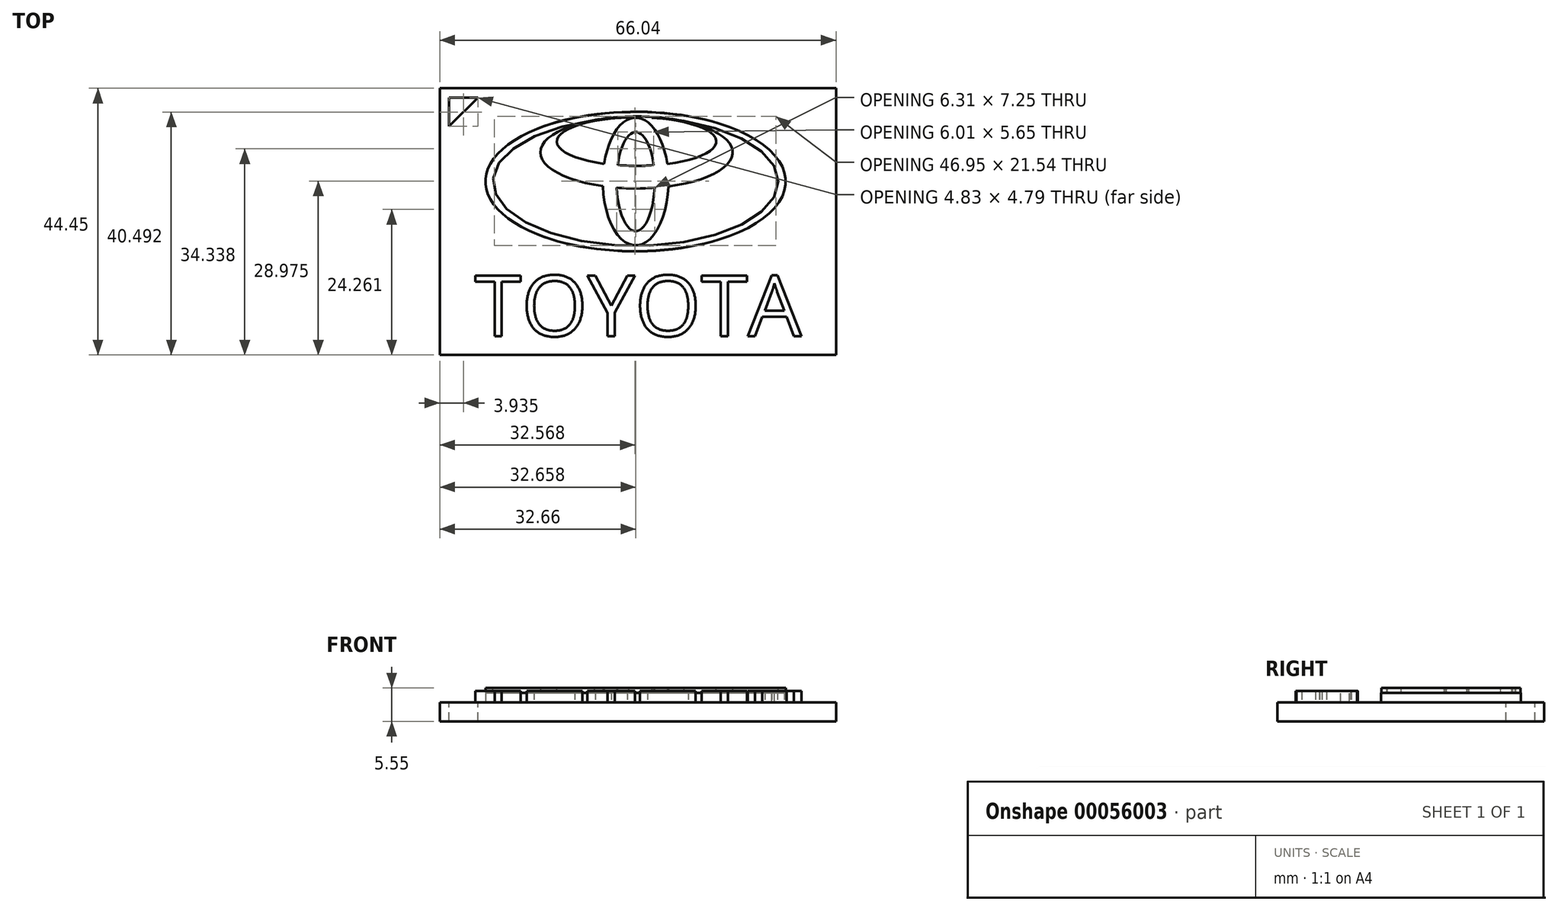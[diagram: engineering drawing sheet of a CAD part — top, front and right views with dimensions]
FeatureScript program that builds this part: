
annotation { "Feature Type Name" : "Feature", "Feature Type Description" : "" }
export const myFeature = defineFeature(function(context is Context, id is Id, definition is map)
    precondition{}
    {
        {
            var Q0;
            Q0=qCreatedBy(makeId("Top.planeOp"),FACE);
            var sketch = newSketch(context, id + "F0", { "sketchPlane" : qUnion([Q0])});
            skLineSegment(sketch, "E0.bottom", {"start": v(-29.53, -28.9) * mm, "end": v(36.5, -28.9) * mm});
            skLineSegment(sketch, "E0.top", {"start": v(-29.53, 15.55) * mm, "end": v(36.5, 15.55) * mm});
            skLineSegment(sketch, "E0.left", {"start": v(-29.53, -28.9) * mm, "end": v(-29.53, 15.55) * mm});
            skLineSegment(sketch, "E0.right", {"start": v(36.5, -28.9) * mm, "end": v(36.5, 15.55) * mm});
            skLineSegment(sketch, "E1", {"start": v(-28, 13.99) * mm, "end": v(-28, 9.2) * mm});
            skLineSegment(sketch, "E2", {"start": v(-28, 9.2) * mm, "end": v(-23.18, 13.99) * mm});
            skLineSegment(sketch, "E3", {"start": v(-23.18, 13.99) * mm, "end": v(-28, 13.99) * mm});
            skEllipse(sketch, "E4", {"center": v(3.1, 0) * mm, "majorRadius": 25.02 * mm, "minorRadius": 11.63 * mm, "majorAxis": v(-1, 0)});
            skText(sketch, "E5", { "text": "TOYOTA", "fontName": "OpenSans-Regular.ttf"});
            skPoint(sketch, "E6", {"position": v(-21.91, 0) * mm});
            skPoint(sketch, "E7", {"position": v(28.13, 0) * mm});
            const initialGuessF0  = {"E5": [-0.0237, -0.02576, 1, 0, 0.01016]};
            skSetInitialGuess(sketch, initialGuessF0);
            skSolve(sketch);
        }
        {
            var Q0;
            Q0=makeQuery(id+"F0.imprint","IMPRINT",FACE,{"disambiguationData":[TD([[makeQuery(id+"F0.imprint","IMPRINT",EDGE,{"derivedFrom":sQuery(id+"F0.wireOp",EDGE,"E0.bottom")}),1.0]])]});
            var Q1;
            Q1=makeQuery(id+"F0.imprint","IMPRINT",FACE,{"disambiguationData":[TD([[makeQuery(id+"F0.imprint","IMPRINT",EDGE,{"derivedFrom":sQuery(id+"F0.wireOp",EDGE,"E4")}),1.0]])]});
            var Q2;
            Q2=makeQuery(id+"F0.imprint","IMPRINT",FACE,{"disambiguationData":[TD([[makeQuery(id+"F0.imprint","IMPRINT",EDGE,{"derivedFrom":sQuery(id+"F0.wireOp",EDGE,"66825ee7-c19d-49c5-bf78-aaec5ceb67ab.sketch_text.stroke-0")}),-1.0]])]});
            var Q3;
            Q3=makeQuery(id+"F0.imprint","IMPRINT",FACE,{"disambiguationData":[TD([[makeQuery(id+"F0.imprint","IMPRINT",EDGE,{"derivedFrom":sQuery(id+"F0.wireOp",EDGE,"66825ee7-c19d-49c5-bf78-aaec5ceb67ab.sketch_text.stroke-25")}),-1.0]])]});
            var Q4;
            Q4=makeQuery(id+"F0.imprint","IMPRINT",FACE,{"disambiguationData":[TD([[makeQuery(id+"F0.imprint","IMPRINT",EDGE,{"derivedFrom":sQuery(id+"F0.wireOp",EDGE,"66825ee7-c19d-49c5-bf78-aaec5ceb67ab.sketch_text.stroke-39")}),-1.0]])]});
            var Q5;
            Q5=makeQuery(id+"F0.imprint","IMPRINT",FACE,{"disambiguationData":[TD([[makeQuery(id+"F0.imprint","IMPRINT",EDGE,{"derivedFrom":sQuery(id+"F0.wireOp",EDGE,"66825ee7-c19d-49c5-bf78-aaec5ceb67ab.sketch_text.stroke-57")}),1.0]])]});
            var Q6;
            Q6=makeQuery(id+"F0.imprint","IMPRINT",FACE,{"disambiguationData":[TD([[makeQuery(id+"F0.imprint","IMPRINT",EDGE,{"derivedFrom":sQuery(id+"F0.wireOp",EDGE,"66825ee7-c19d-49c5-bf78-aaec5ceb67ab.sketch_text.stroke-50")}),1.0]])]});
            var Q7;
            Q7=makeQuery(id+"F0.imprint","IMPRINT",FACE,{"disambiguationData":[TD([[makeQuery(id+"F0.imprint","IMPRINT",EDGE,{"derivedFrom":sQuery(id+"F0.wireOp",EDGE,"66825ee7-c19d-49c5-bf78-aaec5ceb67ab.sketch_text.stroke-72")}),1.0]])]});
            var Q8;
            Q8=makeQuery(id+"F0.imprint","IMPRINT",FACE,{"disambiguationData":[TD([[makeQuery(id+"F0.imprint","IMPRINT",EDGE,{"derivedFrom":sQuery(id+"F0.wireOp",EDGE,"66825ee7-c19d-49c5-bf78-aaec5ceb67ab.sketch_text.stroke-64")}),-1.0]])]});
            var Q9;
            Q9=makeQuery(id+"F0.imprint","IMPRINT",FACE,{"disambiguationData":[TD([[makeQuery(id+"F0.imprint","IMPRINT",EDGE,{"derivedFrom":sQuery(id+"F0.wireOp",EDGE,"66825ee7-c19d-49c5-bf78-aaec5ceb67ab.sketch_text.stroke-88")}),1.0]])]});
            var Q10;
            Q10=makeQuery(id+"F0.imprint","IMPRINT",FACE,{"disambiguationData":[TD([[makeQuery(id+"F0.imprint","IMPRINT",EDGE,{"derivedFrom":sQuery(id+"F0.wireOp",EDGE,"66825ee7-c19d-49c5-bf78-aaec5ceb67ab.sketch_text.stroke-77")}),-1.0]])]});
            var Q11;
            Q11=makeQuery(id+"F0.imprint","IMPRINT",FACE,{"disambiguationData":[TD([[makeQuery(id+"F0.imprint","IMPRINT",EDGE,{"derivedFrom":sQuery(id+"F0.wireOp",EDGE,"E5.sketch_text.stroke-16")}),1.0]])]});
            var Q12;
            Q12=makeQuery(id+"F0.imprint","IMPRINT",FACE,{"disambiguationData":[TD([[makeQuery(id+"F0.imprint","IMPRINT",EDGE,{"derivedFrom":sQuery(id+"F0.wireOp",EDGE,"E5.sketch_text.stroke-8")}),-1.0]])]});
            var Q13;
            Q13=makeQuery(id+"F0.imprint","IMPRINT",FACE,{"disambiguationData":[TD([[makeQuery(id+"F0.imprint","IMPRINT",EDGE,{"derivedFrom":sQuery(id+"F0.wireOp",EDGE,"E5.sketch_text.stroke-0")}),-1.0]])]});
            var Q14;
            Q14=makeQuery(id+"F0.imprint","IMPRINT",FACE,{"disambiguationData":[TD([[makeQuery(id+"F0.imprint","IMPRINT",EDGE,{"derivedFrom":sQuery(id+"F0.wireOp",EDGE,"E5.sketch_text.stroke-24")}),-1.0]])]});
            var Q15;
            Q15=makeQuery(id+"F0.imprint","IMPRINT",FACE,{"disambiguationData":[TD([[makeQuery(id+"F0.imprint","IMPRINT",EDGE,{"derivedFrom":sQuery(id+"F0.wireOp",EDGE,"E5.sketch_text.stroke-33")}),-1.0]])]});
            var Q16;
            Q16=makeQuery(id+"F0.imprint","IMPRINT",FACE,{"disambiguationData":[TD([[makeQuery(id+"F0.imprint","IMPRINT",EDGE,{"derivedFrom":sQuery(id+"F0.wireOp",EDGE,"E5.sketch_text.stroke-41")}),1.0]])]});
            var Q17;
            Q17=makeQuery(id+"F0.imprint","IMPRINT",FACE,{"disambiguationData":[TD([[makeQuery(id+"F0.imprint","IMPRINT",EDGE,{"derivedFrom":sQuery(id+"F0.wireOp",EDGE,"E5.sketch_text.stroke-65")}),1.0]])]});
            var Q18;
            Q18=makeQuery(id+"F0.imprint","IMPRINT",FACE,{"disambiguationData":[TD([[makeQuery(id+"F0.imprint","IMPRINT",EDGE,{"derivedFrom":sQuery(id+"F0.wireOp",EDGE,"E5.sketch_text.stroke-57")}),-1.0]])]});
            var Q19;
            Q19=makeQuery(id+"F0.imprint","IMPRINT",FACE,{"disambiguationData":[TD([[makeQuery(id+"F0.imprint","IMPRINT",EDGE,{"derivedFrom":sQuery(id+"F0.wireOp",EDGE,"E5.sketch_text.stroke-49")}),-1.0]])]});
            extrude(context, id + "F1", {"entities" : qUnion([Q0, Q1, Q2, Q3, Q4, Q5, Q6, Q7, Q8, Q9, Q10, Q11, Q12, Q13, Q14, Q15, Q16, Q17, Q18, Q19]), "oppositeDirection" : true, "depth" : 3.17 * mm});
        }
        {
            var Q0;
            Q0=makeQuery(id+"F0.imprint","IMPRINT",FACE,{"disambiguationData":[TD([[makeQuery(id+"F0.imprint","IMPRINT",EDGE,{"derivedFrom":sQuery(id+"F0.wireOp",EDGE,"66825ee7-c19d-49c5-bf78-aaec5ceb67ab.sketch_text.stroke-0")}),-1.0]])]});
            var Q1;
            Q1=makeQuery(id+"F0.imprint","IMPRINT",FACE,{"disambiguationData":[TD([[makeQuery(id+"F0.imprint","IMPRINT",EDGE,{"derivedFrom":sQuery(id+"F0.wireOp",EDGE,"66825ee7-c19d-49c5-bf78-aaec5ceb67ab.sketch_text.stroke-25")}),-1.0]])]});
            var Q2;
            Q2=makeQuery(id+"F0.imprint","IMPRINT",FACE,{"disambiguationData":[TD([[makeQuery(id+"F0.imprint","IMPRINT",EDGE,{"derivedFrom":sQuery(id+"F0.wireOp",EDGE,"66825ee7-c19d-49c5-bf78-aaec5ceb67ab.sketch_text.stroke-39")}),-1.0]])]});
            var Q3;
            Q3=makeQuery(id+"F0.imprint","IMPRINT",FACE,{"disambiguationData":[TD([[makeQuery(id+"F0.imprint","IMPRINT",EDGE,{"derivedFrom":sQuery(id+"F0.wireOp",EDGE,"66825ee7-c19d-49c5-bf78-aaec5ceb67ab.sketch_text.stroke-64")}),-1.0]])]});
            var Q4;
            Q4=makeQuery(id+"F0.imprint","IMPRINT",FACE,{"disambiguationData":[TD([[makeQuery(id+"F0.imprint","IMPRINT",EDGE,{"derivedFrom":sQuery(id+"F0.wireOp",EDGE,"66825ee7-c19d-49c5-bf78-aaec5ceb67ab.sketch_text.stroke-77")}),-1.0]])]});
            var Q5;
            Q5=makeQuery(id+"F0.imprint","IMPRINT",FACE,{"disambiguationData":[TD([[makeQuery(id+"F0.imprint","IMPRINT",EDGE,{"derivedFrom":sQuery(id+"F0.wireOp",EDGE,"66825ee7-c19d-49c5-bf78-aaec5ceb67ab.sketch_text.stroke-95")}),-1.0]])]});
            var Q6;
            Q6=makeQuery(id+"F0.imprint","IMPRINT",FACE,{"disambiguationData":[TD([[makeQuery(id+"F0.imprint","IMPRINT",EDGE,{"derivedFrom":sQuery(id+"F0.wireOp",EDGE,"E4")}),1.0]])]});
            extrude(context, id + "F2", {"entities" : qUnion([Q0, Q1, Q2, Q3, Q4, Q5, Q6]), "operationType" : NewBodyOperationType.ADD, "depth" : 1.59 * mm});
        }
        {
            var Q0;
            Q0=makeQuery(id+"F2.opExtrude","CAP_FACE",FACE,{"disambiguationData":[OSD([sQuery(id+"F0.wireOp",EDGE,"E4")])],"isStart":false});
            var sketch = newSketch(context, id + "F3", { "sketchPlane" : qUnion([Q0])});
            skSolve(sketch);
        }
        {
            var Q0;
            Q0=makeQuery(id+"F0.imprint","IMPRINT",FACE,{"disambiguationData":[TD([[makeQuery(id+"F0.imprint","IMPRINT",EDGE,{"derivedFrom":sQuery(id+"F0.wireOp",EDGE,"E5.sketch_text.stroke-0")}),-1.0]])]});
            var Q1;
            Q1=makeQuery(id+"F0.imprint","IMPRINT",FACE,{"disambiguationData":[TD([[makeQuery(id+"F0.imprint","IMPRINT",EDGE,{"derivedFrom":sQuery(id+"F0.wireOp",EDGE,"E5.sketch_text.stroke-8")}),-1.0]])]});
            var Q2;
            Q2=makeQuery(id+"F0.imprint","IMPRINT",FACE,{"disambiguationData":[TD([[makeQuery(id+"F0.imprint","IMPRINT",EDGE,{"derivedFrom":sQuery(id+"F0.wireOp",EDGE,"E5.sketch_text.stroke-24")}),-1.0]])]});
            var Q3;
            Q3=makeQuery(id+"F0.imprint","IMPRINT",FACE,{"disambiguationData":[TD([[makeQuery(id+"F0.imprint","IMPRINT",EDGE,{"derivedFrom":sQuery(id+"F0.wireOp",EDGE,"E5.sketch_text.stroke-33")}),-1.0]])]});
            var Q4;
            Q4=makeQuery(id+"F0.imprint","IMPRINT",FACE,{"disambiguationData":[TD([[makeQuery(id+"F0.imprint","IMPRINT",EDGE,{"derivedFrom":sQuery(id+"F0.wireOp",EDGE,"E5.sketch_text.stroke-49")}),-1.0]])]});
            var Q5;
            Q5=makeQuery(id+"F0.imprint","IMPRINT",FACE,{"disambiguationData":[TD([[makeQuery(id+"F0.imprint","IMPRINT",EDGE,{"derivedFrom":sQuery(id+"F0.wireOp",EDGE,"E5.sketch_text.stroke-57")}),-1.0]])]});
            extrude(context, id + "F4", {"entities" : qUnion([Q0, Q1, Q2, Q3, Q4, Q5]), "operationType" : NewBodyOperationType.ADD, "depth" : 1.9 * mm});
        }
        {
            var Q0;
            Q0=makeQuery(id+"F3.imprint","IMPRINT",FACE,{"disambiguationData":[TD([[makeQuery(id+"F3.imprint","IMPRINT",EDGE,{"derivedFrom":makeQuery(id+"F2.opExtrude","CAP_EDGE",EDGE,{"disambiguationData":[OSD([sQuery(id+"F0.wireOp",EDGE,"E4")])],"isStart":false})}),1.0]])]});
            var sketch = newSketch(context, id + "F5", { "sketchPlane" : qUnion([Q0])});
            skEllipse(sketch, "E8", {"center": v(3.13, 0) * mm, "majorRadius": 25.16 * mm, "minorRadius": 11.6 * mm, "majorAxis": v(-1, 0)});
            skEllipse(sketch, "E9", {"center": v(3.13, 0) * mm, "majorRadius": 23.78 * mm, "minorRadius": 10.7 * mm, "majorAxis": v(-1, 0)});
            skEllipse(sketch, "E10", {"center": v(3.26, 6.66) * mm, "majorRadius": 13.3 * mm, "minorRadius": 4.05 * mm, "majorAxis": v(1, 0)});
            skEllipse(sketch, "E11", {"center": v(3.26, 4.85) * mm, "majorRadius": 16.02 * mm, "minorRadius": 6 * mm, "majorAxis": v(-1, 0)});
            skEllipse(sketch, "E12", {"center": v(3.13, 0) * mm, "majorRadius": 8.27 * mm, "minorRadius": 3.18 * mm, "majorAxis": v(0, -1)});
            skEllipse(sketch, "E13", {"center": v(3.13, 0) * mm, "majorRadius": 10.65 * mm, "minorRadius": 5.47 * mm, "majorAxis": v(0, -1)});
            skSolve(sketch);
        }
        {
            var Q0;
            {var subQ0=sQuery(id+"F5.wireOp",EDGE,"E12");var subQ1=sQuery(id+"F5.wireOp",EDGE,"E10");var subQ2=makeQuery(id+"F5.imprint","INTERSECT",VERTEX,{"disambiguationData":[OD(0.0)],"derivedFrom":[subQ1,subQ0]});Q0=makeQuery(id+"F5.imprint","IMPRINT",FACE,{"disambiguationData":[TD([[makeQuery(id+"F5.imprint","IMPRINT",EDGE,{"disambiguationData":[TD([[subQ2,-1.0]])],"derivedFrom":subQ1}),-1.0]])]});}
            var Q1;
            {var subQ0=sQuery(id+"F5.wireOp",EDGE,"E12");var subQ1=sQuery(id+"F5.wireOp",EDGE,"E10");var subQ2=makeQuery(id+"F5.imprint","INTERSECT",VERTEX,{"disambiguationData":[OD(1.0)],"derivedFrom":[subQ1,subQ0]});Q1=makeQuery(id+"F5.imprint","IMPRINT",FACE,{"disambiguationData":[TD([[makeQuery(id+"F5.imprint","IMPRINT",EDGE,{"disambiguationData":[TD([[subQ2,-1.0]])],"derivedFrom":subQ1}),-1.0]])]});}
            var Q2;
            {var subQ0=sQuery(id+"F5.wireOp",EDGE,"E13");var subQ1=sQuery(id+"F5.wireOp",EDGE,"E10");var subQ2=makeQuery(id+"F5.imprint","INTERSECT",VERTEX,{"disambiguationData":[OD(0.0)],"derivedFrom":[subQ1,subQ0]});Q2=makeQuery(id+"F5.imprint","IMPRINT",FACE,{"disambiguationData":[TD([[makeQuery(id+"F5.imprint","IMPRINT",EDGE,{"disambiguationData":[TD([[subQ2,-1.0]])],"derivedFrom":subQ1}),-1.0]])]});}
            var Q3;
            {var subQ0=sQuery(id+"F5.wireOp",EDGE,"E13");var subQ1=sQuery(id+"F5.wireOp",EDGE,"E10");var subQ2=makeQuery(id+"F5.imprint","INTERSECT",VERTEX,{"disambiguationData":[OD(0.0)],"derivedFrom":[subQ1,subQ0]});Q3=makeQuery(id+"F5.imprint","IMPRINT",FACE,{"disambiguationData":[TD([[makeQuery(id+"F5.imprint","IMPRINT",EDGE,{"disambiguationData":[TD([[subQ2,-1.0]])],"derivedFrom":subQ1}),1.0]])]});}
            var Q4;
            {var subQ0=sQuery(id+"F5.wireOp",EDGE,"E10");var subQ1=sQuery(id+"F5.wireOp",EDGE,"E9");var subQ2=makeQuery(id+"F5.imprint","INTERSECT",VERTEX,{"disambiguationData":[OD(0.0)],"derivedFrom":[subQ1,subQ0]});Q4=makeQuery(id+"F5.imprint","IMPRINT",FACE,{"disambiguationData":[TD([[makeQuery(id+"F5.imprint","IMPRINT",EDGE,{"disambiguationData":[TD([[subQ2,1.0]])],"derivedFrom":subQ1}),1.0]])]});}
            var Q5;
            {var subQ0=sQuery(id+"F5.wireOp",EDGE,"E10");var subQ1=sQuery(id+"F5.wireOp",EDGE,"E9");var subQ2=makeQuery(id+"F5.imprint","INTERSECT",VERTEX,{"disambiguationData":[OD(1.0)],"derivedFrom":[subQ1,subQ0]});Q5=makeQuery(id+"F5.imprint","IMPRINT",FACE,{"disambiguationData":[TD([[makeQuery(id+"F5.imprint","IMPRINT",EDGE,{"disambiguationData":[TD([[subQ2,-1.0]])],"derivedFrom":subQ1}),1.0]])]});}
            var Q6;
            {var subQ4=sQuery(id+"F5.wireOp",EDGE,"E8");var subQ5=makeQuery(id+"F3.imprint","IMPRINT",EDGE,{"derivedFrom":makeQuery(id+"F2.opExtrude","CAP_EDGE",EDGE,{"disambiguationData":[OSD([sQuery(id+"F0.wireOp",EDGE,"E4")])],"isStart":false})});var subQ8=makeQuery(id+"F5.imprint","INTERSECT",VERTEX,{"disambiguationData":[OD(0.0)],"derivedFrom":[subQ5,subQ4]});Q6=makeQuery(id+"F5.imprint","IMPRINT",FACE,{"disambiguationData":[TD([[makeQuery(id+"F5.imprint","IMPRINT",EDGE,{"disambiguationData":[TD([[subQ8,1.0]])],"derivedFrom":subQ4}),1.0]])]});}
            var Q7;
            {var subQ0=sQuery(id+"F5.wireOp",EDGE,"E12");var subQ1=sQuery(id+"F5.wireOp",EDGE,"E11");var subQ2=makeQuery(id+"F5.imprint","INTERSECT",VERTEX,{"disambiguationData":[OD(0.0)],"derivedFrom":[subQ1,subQ0]});Q7=makeQuery(id+"F5.imprint","IMPRINT",FACE,{"disambiguationData":[TD([[makeQuery(id+"F5.imprint","IMPRINT",EDGE,{"disambiguationData":[TD([[subQ2,1.0]])],"derivedFrom":subQ1}),-1.0]])]});}
            extrude(context, id + "F6", {"entities" : qUnion([Q0, Q1, Q2, Q3, Q4, Q5, Q6, Q7]), "depth" : 0.8 * mm});
        }
    });
